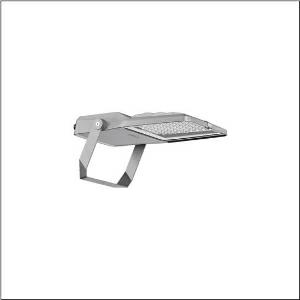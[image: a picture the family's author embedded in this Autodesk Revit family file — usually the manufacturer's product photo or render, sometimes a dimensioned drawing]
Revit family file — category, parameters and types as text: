
# Revit family: floodlight_fl_21_mini___pl33t_5xa7772b4f1a_1cc4
name_source: partatom
category: Lighting Fixtures
units: mm (PartAtom-declared; Revit-internal decimal feet)

## family parameters
Cut with Voids When Loaded = No
Host = Face
Light Source = No
Part Type = Normal
Room Calculation Point = No
Round Connector Dimension = Use Diameter
Shared = No

## types (1)
- --- (1 x LED, 6420 lm, 45.5 W, 4000K)
    Apparent Load = 46 VA
    CIE Flux Codes = 26 75 99 100 100
    Color Rendering = 70
    Color Temperature = 4000K
    Default Elevation = 1800 mm
    Description = Floodlight FL 21 mini, floodlight, primary light control with lens, of PMMA, primary optical cover: protective disc, of toughened safety glass, transparent, light distribution: PL33T, light emission: direct distribution, installation type: surface-mounted, LED, High Power LED, rated luminous flux: 6.420lm, luminous efficacy: 141lm/W, light colour: 740, colour temperature: 4000K, control gear: ECG iQ, control: Street-Remote, Auto-Match, Temp-Guard, Night-Set, Smart-Wire, Desk-Remote (wireless, voltage-free reading and setting of iQ features in the workshop via application-optimized NFC function/RFID function), optimised constant luminous flux control (CLO 2.0), with terminal, 6-pole, mains connection: 220..240V, AC, 50/60Hz, start of lifetime: 46W, end of lifetime: 48W, reduction: 22W, luminaire housing, of diecast aluminium, powder-coated, Siteco® metallic grey (DB 702S), corrosivity category C5 according to DIN EN ISO 12944, mounting bracket, of steel, galvanised, powder-coated, Siteco® metallic grey (DB 702S), protection rating (complete): IP66, insulation class (complete): insulation class II (safety insulation), certification: CE, ENEC, VDE, protection symbol: D, impact resistance: IK08, permissible operating ambient temperature: -40..+40°C, permissible operating ambient temperature for outdoor applications: -40..+50°C, standard: DIN EN 12944, packaging unit: 1 piece

Light Distribution: PL33T
    Height = 70 mm
    Lamp = 1 x LED
    Lamp Light Flux = 6420 lm
    Lamp Power = 45.5 W
    Lamp count = 1
    Length = 485 mm
    Luminous efficacy = 141 lm/W
    Manufacturer = Siteco
    ModVariant = No
    Model = 5XA7772B4F1A
    Number of Poles = 1
    OnlyDefault = Yes
    Power Factor = 1
    Product Name = Floodlight FL 21 mini | PL33T
    Product group = floodlight | pylon top
    ProductGroupID = 6101
    Protection Class = Protection class II
    Protection Degree = IP 66
    RLX_Detail_Level = 1
    RlxData = <blob elided: 95957 chars, md5=02877b53>
    Socket = socket
    Standby Power = 0 W
    System Light Flux = 6420 lm
    System Power = 46 W
    Type Comments = factory setting: luminous flux: 100 % | dim-lin: 254 | 463 mA
    Type Image = l_1006845.jpg
    URL = http://relux.com
    VarID = @adj_059981
    Voltage = 0 V
    Weight = 0.00 kg
    Width = 337 mm

## geometry (parser evidence)
native form markers: Blend x4, Sweep x13
no freeform markers — native parametric forms only
